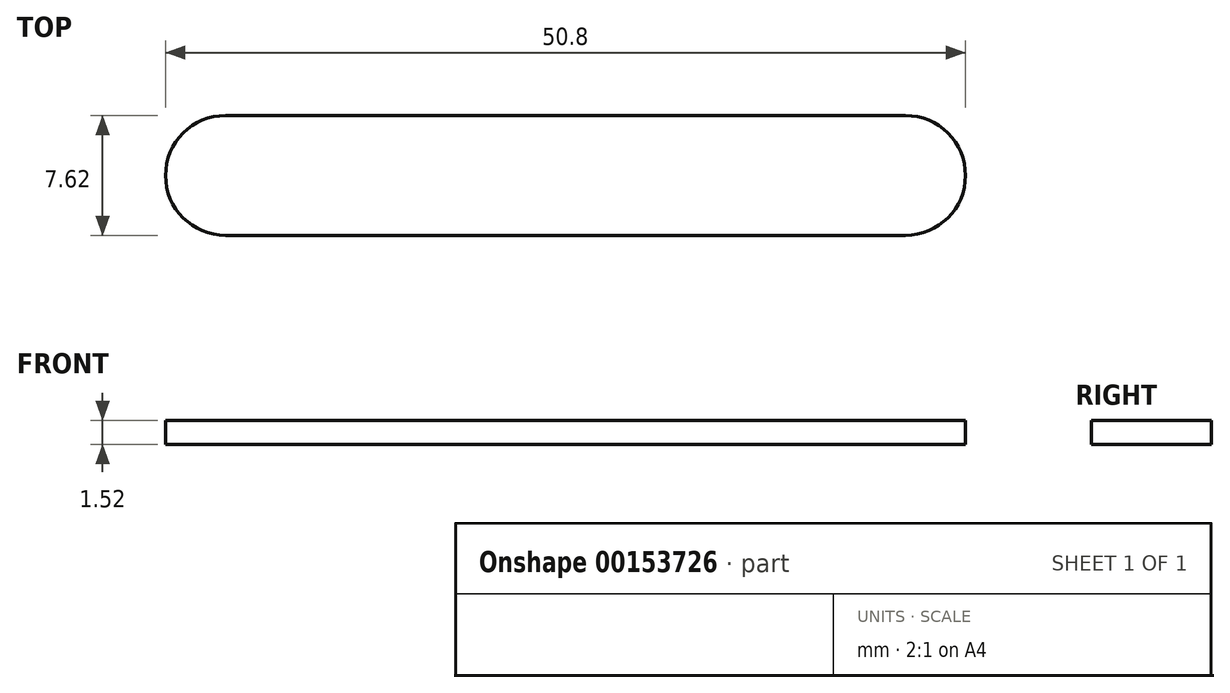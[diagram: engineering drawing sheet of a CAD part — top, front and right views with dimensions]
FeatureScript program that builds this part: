
annotation { "Feature Type Name" : "Feature", "Feature Type Description" : "" }
export const myFeature = defineFeature(function(context is Context, id is Id, definition is map)
    precondition{}
    {
        {
            var Q0;
            Q0=qCreatedBy(makeId("Top.planeOp"),FACE);
            var sketch = newSketch(context, id + "F0", { "sketchPlane" : qUnion([Q0])});
            skLineSegment(sketch, "E0.bottom", {"start": v(-25.4, 3.81) * mm, "end": v(25.4, 3.8) * mm});
            skLineSegment(sketch, "E0.top", {"start": v(-25.4, -3.8) * mm, "end": v(25.4, -3.81) * mm});
            skLineSegment(sketch, "E0.left", {"start": v(-25.4, 3.8) * mm, "end": v(-25.4, -3.8) * mm});
            skLineSegment(sketch, "E0.right", {"start": v(25.4, 3.8) * mm, "end": v(25.4, -3.8) * mm});
            skPoint(sketch, "E1", {"position": v(-25.4, 0) * mm});
            skPoint(sketch, "E2", {"position": v(0, 3.81) * mm});
            skSolve(sketch);
        }
        {
            var Q0;
            Q0 = qSketchRegion(id + "F0", true);
            extrude(context, id + "F1", {"entities" : qUnion([Q0]), "depth" : 1.52 * mm});
        }
        {
            var Q0;
            Q0=makeQuery(id+"F1.opExtrude","SWEPT_EDGE",EDGE,{"disambiguationData":[OSD([sQuery(id+"F0.wireOp",EDGE,"E0.bottom"),sQuery(id+"F0.wireOp",EDGE,"E0.right")])]});
            var Q1;
            Q1=makeQuery(id+"F1.opExtrude","SWEPT_EDGE",EDGE,{"disambiguationData":[OSD([sQuery(id+"F0.wireOp",EDGE,"E0.top"),sQuery(id+"F0.wireOp",EDGE,"E0.right")])]});
            var Q2;
            Q2=makeQuery(id+"F1.opExtrude","SWEPT_EDGE",EDGE,{"disambiguationData":[OSD([sQuery(id+"F0.wireOp",EDGE,"E0.top"),sQuery(id+"F0.wireOp",EDGE,"E0.left")])]});
            var Q3;
            Q3=makeQuery(id+"F1.opExtrude","SWEPT_EDGE",EDGE,{"disambiguationData":[OSD([sQuery(id+"F0.wireOp",EDGE,"E0.bottom"),sQuery(id+"F0.wireOp",EDGE,"E0.left")])]});
            fillet(context, id + "F2", {"entities" : qUnion([Q0, Q1, Q2, Q3]), "radius" : 3.8 * mm, "tangentPropagation" : true, "allowEdgeOverflow" : false});
        }
    });
